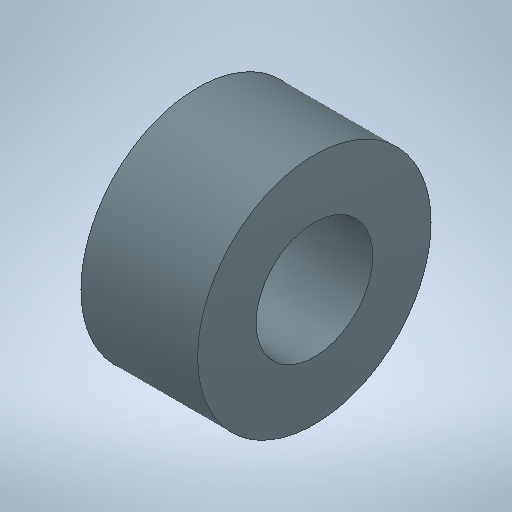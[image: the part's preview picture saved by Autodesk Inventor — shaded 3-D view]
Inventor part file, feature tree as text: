
AUTODESK INVENTOR PART (.ipt)
format: ipt  version: 2025.1 (Build 291241000, 241)  size: 262,144 bytes
history: native  units: mm
features: revolve x1, sketch x1
ambient origin geometry x8: Origin, YZ Plane, XZ Plane, XY Plane, X Axis, Y Axis, Z Axis, Center Point
bodies: Solid1 (feature_tree)
feature tree (2):
  revolve  "Revolution1"  [1 undecoded]
  sketch  "Sketch1"  dims[d0=6.0mm d1=12.0mm d2=6.0mm d3=90.0deg]
note: 1 required parameter value undecoded (feature->parameter linkage not recoverable at this tier; creation-order binding heuristic only, values carry confidence <= 0.55)
